# Revit family: Furniture_Office-Chairs_Flokk_Giroflex-313
name_source: partatom
category: Furniture
units: mm (PartAtom-declared; Revit-internal decimal feet)

## family parameters
Always vertical = Yes
Cut with Voids When Loaded = No
OmniClass Number = 23.40.20.14.14.11
OmniClass Title = Chairs
Room Calculation Point = No
Shared = No
Work Plane-Based = No

## types (1)
- Giroflex 313
    AssetType = Movable
    BIMObjectName = Furniture_Office-Chairs_Flokk_Giroflex-313
    Brand = Flokk
    Category = Giroflex
    Color = Various
    Cost = 0 $
    Default Elevation = 0 mm  [stored 0 ft]
    Description = Sit down, lean back and feel good. The giroflex 313chair is as flexible as its users are different.

The Giroflex 313 is perfect for any place where different people need to sit comfortably to work, being a conference room, co-wrking spaces, or the home office.

The Balance Move system specially developed by Giroflex. Right from the start it provides maximum seating comfort and ease of operation. The seat and back align perfectly with the user’s body weight. Only the seat height is adjusted manually. The chair does the rest.

With the backrest mesh runner this model is delivered with, the user will experience a light and breazy seating with good support when leaning back. You can also choose from a elegant range of armrests. Either in a classic black matte plastic, or a more premium recycled aluminium with four different finishes.
    Designer = Paolo Fancelli
    DurationUnit = Year
    Features = The giroflex 313 range is designed with sustainability in mind. And its Cradle-to-Cradle certification is proof positive of this.
    IfcExportAs = IfcFurnishingElementType
    IfcExportType = CHAIR
    LowestSeatingHeight = 500 mm  [stored 1.64042 ft]
    MainColor = Various
    Manufacturer = Flokk
    ManufacturerName = Flokk
    ManufacturerURL = https://www.flokk.com
    Material = Plastic, Metal and Textile
    Model = Giroflex 313
    ModelNumber = 313-4039
    NBSDescription = Stacking chairs
    NBSReference = 45-35-20/355
    Name = Giroflex 313
    NominalDepth = 670 mm
    NominalLength = 700 mm
    OfficeChairQuaternaryMaterial = Black RAL 9005
    ProductDatasheet = https://flokkplatformprod.blob.core.windows.net
    ProductInformation = The giroflex 313 is ready for action. This comfortable chair automatically adjusts to accommodate users, perfect when several employees share the same workstation.
    SeatingHeight = 500 mm  [stored 1.64042 ft]
    Shape = Sculptured
    Size = 700x670x945 mm
    URL = https://store.flokk.com
    Uniclass2 = Pr_40_50_12_51
    Uniclass2015Description = Meeting room chairs
    Uniclass2015Reference = Pr_40_50_12_51
    Version = 1
    VersionDate = 10/01/2022
    WarrantyDurationUnit = Year

note: [stored X ft] marks values corroborated as IEEE doubles in the binary element streams (Revit-internal decimal feet)

## geometry (parser evidence)
native form markers: Sweep x5
no freeform markers — native parametric forms only
